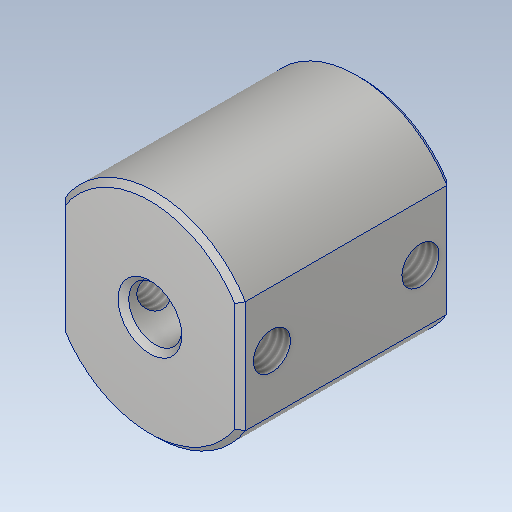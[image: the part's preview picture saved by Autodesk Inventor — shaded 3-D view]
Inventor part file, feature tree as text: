
AUTODESK INVENTOR PART (.ipt)
format: ipt  version: 2020 (Build 240168000, 168)  size: 182,784 bytes
history: native  units: mm
features: thread x4, extrude x3, sketch x3, chamfer x2, mirror x1, hole x1
ambient origin geometry x8: Origin, YZ Plane, XZ Plane, XY Plane, X Axis, Y Axis, Z Axis, Center Point
bodies: Solid1 (feature_tree)
feature tree (14):
  extrude  "Extrusion1"  Depth=20.0mm TaperAngle=0.0deg
  extrude  "Extrusion3"  Depth=3.0mm
  sketch  "Sketch4"  dims[d7=8.0mm d8=0.0mm d9=3.0mm]
  extrude  "Extrusion5"  Depth=3.0mm
  mirror  "Mirror1"
  chamfer  "Chamfer1"  Distance=3.0mm
  chamfer  "Chamfer2"  Distance=21.25mm
  hole  "Hole1"  [1 undecoded]
  thread  "Thread5"  [1 undecoded]
  thread  "Thread6"  [1 undecoded]
  thread  "Thread7"  [1 undecoded]
  thread  "Thread8"  [1 undecoded]
  sketch  "Sketch1"  dims[d0=20.0mm d1=20.0mm d2=0.0mm]
  sketch  "Sketch5"  dims[d10=3.0mm d11=3.0mm d12=3.0mm d17=21.25mm d18=0.0mm d19=0.5mm d20=2.0mm d21=45.0deg d30=0.5mm d31=2.0mm d32=45.0deg d33=3.5mm d34=6.0mm d35=4.0mm d36=2.0mm d37=90.0deg d38=8.0mm d39=120.0deg d40=10.0mm d41=0.0mm d42=10.0mm d43=0.0mm d44=10.0mm d45=0.0mm d46=10.0mm d47=0.0mm d48=8.5mm d49=5.0mm]
note: 5 required parameter values undecoded (feature->parameter linkage not recoverable at this tier; creation-order binding heuristic only, values carry confidence <= 0.55)
